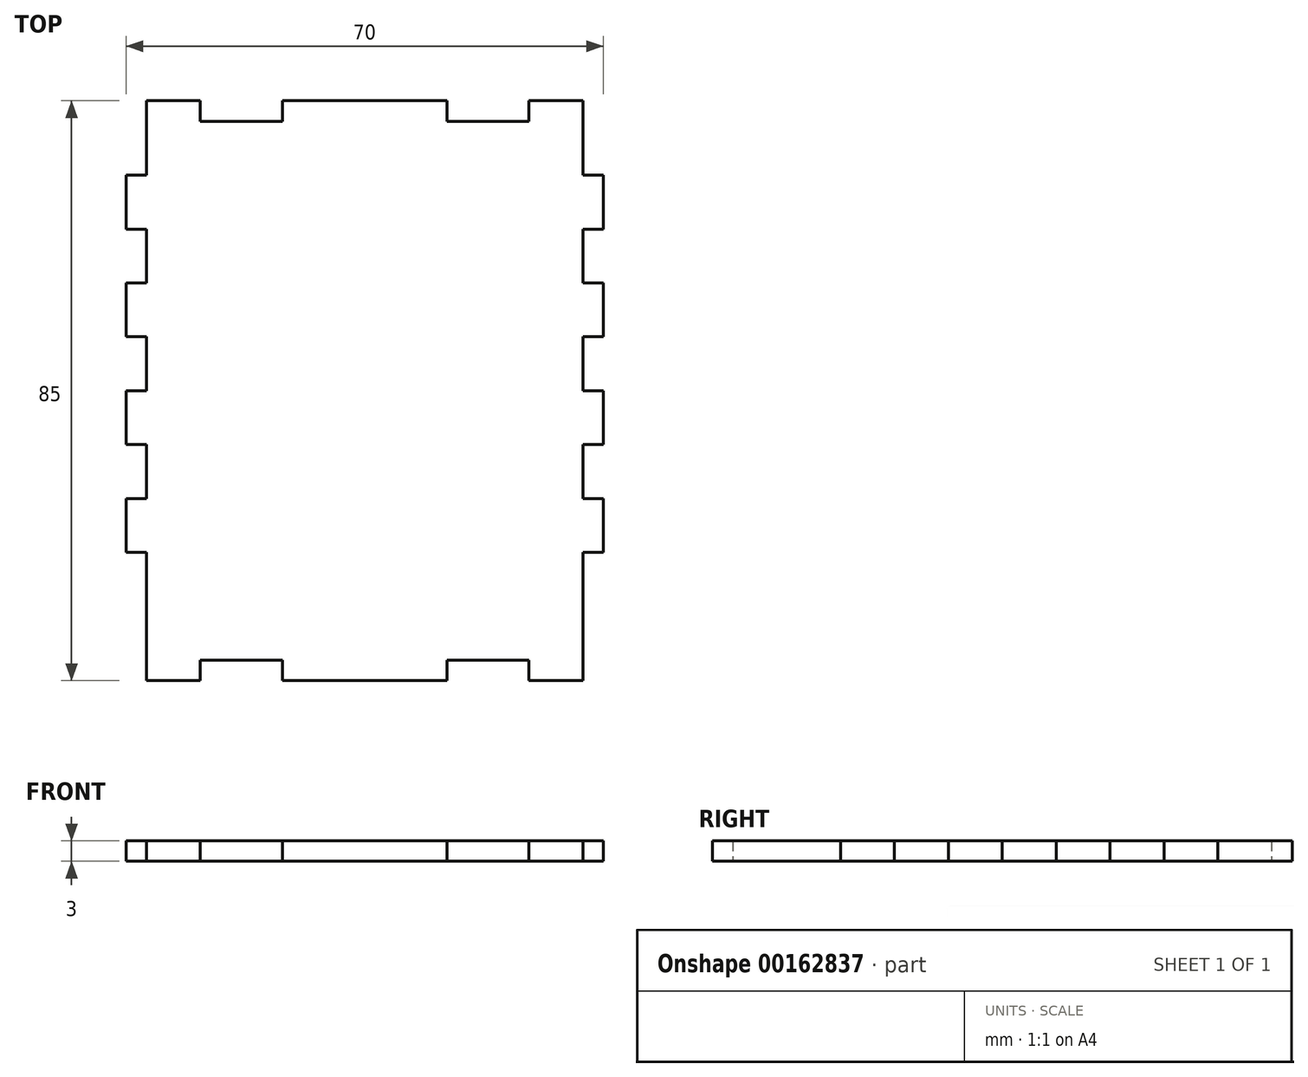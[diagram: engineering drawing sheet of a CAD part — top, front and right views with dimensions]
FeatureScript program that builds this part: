
annotation { "Feature Type Name" : "Feature", "Feature Type Description" : "" }
export const myFeature = defineFeature(function(context is Context, id is Id, definition is map)
    precondition{}
    {
        {
            var Q0;
            Q0=qCreatedBy(makeId("Top.planeOp"),FACE);
            var sketch = newSketch(context, id + "F0", { "sketchPlane" : qUnion([Q0])});
            skLineSegment(sketch, "E0.top", {"start": v(-32, -42.5) * mm, "end": v(-24.1, -42.5) * mm});
            skLineSegment(sketch, "E0.left", {"start": v(-35, 31.6) * mm, "end": v(-35, 23.7) * mm});
            skLineSegment(sketch, "E1.top", {"start": v(-24.1, -39.5) * mm, "end": v(-12.05, -39.5) * mm});
            skLineSegment(sketch, "E1.left", {"start": v(-32, 39.5) * mm, "end": v(-32, 31.6) * mm});
            skLineSegment(sketch, "E2", {"start": v(-24.1, -39.5) * mm, "end": v(-24.1, -42.5) * mm});
            skLineSegment(sketch, "E3", {"start": v(-12.05, -39.5) * mm, "end": v(-12.05, -42.5) * mm});
            skLineSegment(sketch, "E4", {"start": v(24.1, -39.5) * mm, "end": v(24.1, -42.5) * mm});
            skLineSegment(sketch, "E5", {"start": v(12.05, -39.5) * mm, "end": v(12.05, -42.5) * mm});
            skLineSegment(sketch, "E6.trimOffspring", {"start": v(-12.05, -42.5) * mm, "end": v(12.05, -42.5) * mm});
            skLineSegment(sketch, "E7.trimOffspring", {"start": v(24.1, -42.5) * mm, "end": v(32, -42.5) * mm});
            skLineSegment(sketch, "E8.trimOffspring", {"start": v(12.05, -39.5) * mm, "end": v(24.1, -39.5) * mm});
            skLineSegment(sketch, "E9", {"start": v(-32, -39.5) * mm, "end": v(-32, -42.5) * mm});
            skLineSegment(sketch, "E10", {"start": v(-35, -23.7) * mm, "end": v(-32, -23.7) * mm});
            skPoint(sketch, "E11.orphan", {"position": v(-35, -42.5) * mm});
            skLineSegment(sketch, "E12", {"start": v(-35, -15.8) * mm, "end": v(-32, -15.8) * mm});
            skLineSegment(sketch, "E13", {"start": v(-35, -7.9) * mm, "end": v(-32, -7.9) * mm});
            skLineSegment(sketch, "E14", {"start": v(-35, 0) * mm, "end": v(-32, 0) * mm});
            skLineSegment(sketch, "E15", {"start": v(-35, 7.9) * mm, "end": v(-32, 7.9) * mm});
            skLineSegment(sketch, "E16", {"start": v(-35, 15.8) * mm, "end": v(-32, 15.8) * mm});
            skLineSegment(sketch, "E17", {"start": v(-35, 23.7) * mm, "end": v(-32, 23.7) * mm});
            skLineSegment(sketch, "E18", {"start": v(-35, 31.6) * mm, "end": v(-32, 31.6) * mm});
            skLineSegment(sketch, "E19.trimOffspring", {"start": v(-35, -15.8) * mm, "end": v(-35, -23.7) * mm});
            skLineSegment(sketch, "E20.trimOffspring", {"start": v(-35, 0) * mm, "end": v(-35, -7.9) * mm});
            skLineSegment(sketch, "E21.trimOffspring", {"start": v(-35, 15.8) * mm, "end": v(-35, 7.9) * mm});
            skLineSegment(sketch, "E22", {"start": v(-32, 39.5) * mm, "end": v(-32, 42.5) * mm});
            skLineSegment(sketch, "E23.MirrorCS", {"start": v(12.05, 39.5) * mm, "end": v(12.05, 42.5) * mm});
            skLineSegment(sketch, "E24.MirrorCS", {"start": v(-12.05, 39.5) * mm, "end": v(-12.05, 42.5) * mm});
            skLineSegment(sketch, "E25.MirrorCS", {"start": v(-24.1, 39.5) * mm, "end": v(-24.1, 42.5) * mm});
            skLineSegment(sketch, "E26.MirrorCS", {"start": v(24.1, 39.5) * mm, "end": v(24.1, 42.5) * mm});
            skLineSegment(sketch, "E27.MirrorCS", {"start": v(12.05, 39.5) * mm, "end": v(24.1, 39.5) * mm});
            skLineSegment(sketch, "E28.MirrorCS", {"start": v(24.1, 42.5) * mm, "end": v(32, 42.5) * mm});
            skLineSegment(sketch, "E29.MirrorCS", {"start": v(-24.1, 39.5) * mm, "end": v(-12.05, 39.5) * mm});
            skPoint(sketch, "E30.MirrorP", {"position": v(-35, 42.5) * mm});
            skLineSegment(sketch, "E31.MirrorCS", {"start": v(-12.05, 42.5) * mm, "end": v(12.05, 42.5) * mm});
            skLineSegment(sketch, "E32.MirrorCS", {"start": v(-32, 42.5) * mm, "end": v(-24.1, 42.5) * mm});
            skLineSegment(sketch, "E33.trimOffspring", {"start": v(-32, 23.7) * mm, "end": v(-32, 15.8) * mm});
            skLineSegment(sketch, "E34.trimOffspring", {"start": v(-32, 7.9) * mm, "end": v(-32, 0) * mm});
            skLineSegment(sketch, "E35.trimOffspring", {"start": v(-32, -7.9) * mm, "end": v(-32, -15.8) * mm});
            skLineSegment(sketch, "E36.trimOffspring", {"start": v(-32, -23.7) * mm, "end": v(-32, -39.5) * mm});
            skLineSegment(sketch, "E37.MirrorCS", {"start": v(32, 39.5) * mm, "end": v(32, 42.5) * mm});
            skLineSegment(sketch, "E38.MirrorCS", {"start": v(35, 7.9) * mm, "end": v(32, 7.9) * mm});
            skLineSegment(sketch, "E39.MirrorCS", {"start": v(35, 23.7) * mm, "end": v(32, 23.7) * mm});
            skLineSegment(sketch, "E40.MirrorCS", {"start": v(35, -23.7) * mm, "end": v(32, -23.7) * mm});
            skLineSegment(sketch, "E41.MirrorCS", {"start": v(32, -39.5) * mm, "end": v(32, -42.5) * mm});
            skLineSegment(sketch, "E42.MirrorCS", {"start": v(35, 31.6) * mm, "end": v(32, 31.6) * mm});
            skLineSegment(sketch, "E43.MirrorCS", {"start": v(35, -15.8) * mm, "end": v(32, -15.8) * mm});
            skLineSegment(sketch, "E44.MirrorCS", {"start": v(35, 15.8) * mm, "end": v(32, 15.8) * mm});
            skLineSegment(sketch, "E45.MirrorCS", {"start": v(35, -7.9) * mm, "end": v(32, -7.9) * mm});
            skLineSegment(sketch, "E46.MirrorCS", {"start": v(32, 39.5) * mm, "end": v(32, 31.6) * mm});
            skLineSegment(sketch, "E47.MirrorCS", {"start": v(35, 0) * mm, "end": v(32, 0) * mm});
            skLineSegment(sketch, "E48.MirrorCS", {"start": v(32, -7.9) * mm, "end": v(32, -15.8) * mm});
            skLineSegment(sketch, "E49.MirrorCS", {"start": v(35, -15.8) * mm, "end": v(35, -23.7) * mm});
            skLineSegment(sketch, "E50.MirrorCS", {"start": v(35, 15.8) * mm, "end": v(35, 7.9) * mm});
            skLineSegment(sketch, "E51.MirrorCS", {"start": v(32, 23.7) * mm, "end": v(32, 15.8) * mm});
            skLineSegment(sketch, "E52.MirrorCS", {"start": v(35, 0) * mm, "end": v(35, -7.9) * mm});
            skPoint(sketch, "E53.MirrorP", {"position": v(35, -42.5) * mm});
            skLineSegment(sketch, "E54.MirrorCS", {"start": v(32, -23.7) * mm, "end": v(32, -39.5) * mm});
            skPoint(sketch, "E55.MirrorP", {"position": v(35, 42.5) * mm});
            skLineSegment(sketch, "E56.MirrorCS", {"start": v(35, 31.6) * mm, "end": v(35, 23.7) * mm});
            skLineSegment(sketch, "E57.MirrorCS", {"start": v(32, 7.9) * mm, "end": v(32, 0) * mm});
            skPoint(sketch, "E58.orphan", {"position": v(32, 39.5) * mm});
            skPoint(sketch, "E59.orphan", {"position": v(32, -39.5) * mm});
            skSolve(sketch);
        }
        {
            var Q0;
            Q0=qSketchRegion(id+"F0",true);
            extrude(context, id + "F1", {"entities" : qUnion([Q0]), "depth" : 3 * mm});
        }
    });
